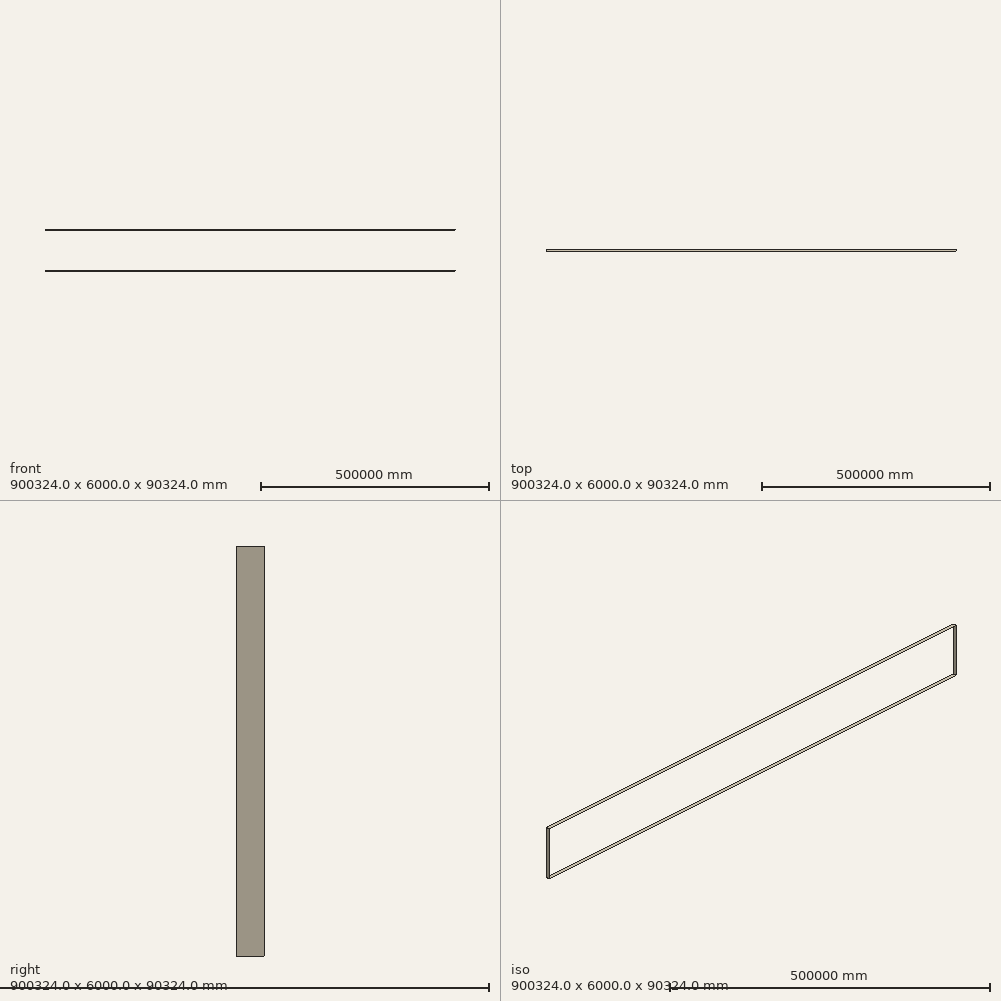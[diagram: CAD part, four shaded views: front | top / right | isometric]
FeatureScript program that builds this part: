
annotation { "Feature Type Name" : "Feature", "Feature Type Description" : "" }
export const myFeature = defineFeature(function(context is Context, id is Id, definition is map)
    precondition{}
    {
        {
            var Q0;
            Q0=qCreatedBy(makeId("Front.planeOp"),FACE);
            var sketch = newSketch(context, id + "F0", { "sketchPlane" : qUnion([Q0])});
            skLineSegment(sketch, "E0.bottom", {"start": v(-450000, -45000) * mm, "end": v(450000, -45000) * mm});
            skLineSegment(sketch, "E0.top", {"start": v(-450000, 45000) * mm, "end": v(450000, 45000) * mm});
            skLineSegment(sketch, "E0.left", {"start": v(-450000, -45000) * mm, "end": v(-450000, 45000) * mm});
            skLineSegment(sketch, "E0.right", {"start": v(450000, -45000) * mm, "end": v(450000, 45000) * mm});
            skPoint(sketch, "E0.middle", {"position": v(0, 0) * mm});
            skLineSegment(sketch, "E1.0", {"start": v(-450162, 45162) * mm, "end": v(450162, 45162) * mm});
            skLineSegment(sketch, "E1.1", {"start": v(-450162, -45162) * mm, "end": v(-450162, 45162) * mm});
            skLineSegment(sketch, "E1.2", {"start": v(-450162, -45162) * mm, "end": v(450162, -45162) * mm});
            skLineSegment(sketch, "E1.3", {"start": v(450162, -45162) * mm, "end": v(450162, 45162) * mm});
            skSolve(sketch);
        }
        {
            var Q0;
            Q0 = qSketchRegion(id + "F0", true);
            extrude(context, id + "F1", {"entities" : qUnion([Q0]), "depth" : 6000 * mm});
        }
    });
